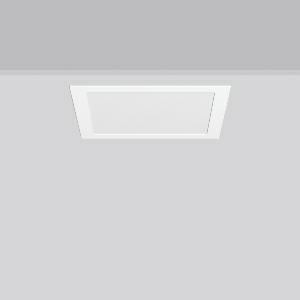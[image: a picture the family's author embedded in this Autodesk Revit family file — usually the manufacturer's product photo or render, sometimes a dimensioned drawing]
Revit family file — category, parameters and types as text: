
# Revit family: toledo_flat_square_e_901488_002_76_2574
name_source: partatom
category: Lighting Fixtures
units: mm (PartAtom-declared; Revit-internal decimal feet)

## family parameters
Cut with Voids When Loaded = No
Host = Face
Light Source = No
Part Type = Normal
Room Calculation Point = No
Round Connector Dimension = Use Diameter
Shared = No

## types (1)
- TOLEDO FLAT square E (1 x LED Modul 830, 2150 lm, 3000)
    Apparent Load = 21 VA
    CIE Flux Codes = 48 80 96 100 100
    Color Rendering = 80
    Color Temperature = 3000
    Default Elevation = 1800 mm
    Description = Series: TOLEDO FLAT square
Ultra thin recessed downlight. Housing: die-cast aluminium. Light guide and diffuser made of non-yellowing PMMA, opal matt. Ceiling installation with spring system. Mounting depth depends on ceiling strength. Suitable for through-wiring with separately available accessories. Surface mounted housing as accessory for all sizes. Retrofittable decorative cylinders made of chintz fabric as accessory, optional with satin finish plastic diffuser. Through-wiring box (5 pole) available as accessory. 
Colour: white
Length: 300 mm
Width: 300 mm
Height: 3 mm
Cut-out length: 280 mm
Cut-out width: 280 mm
Recess height: 31-56 mm
Luminaire: recess height: 31-51 mm
Lamp: LED
Socket: without socket
Colour temperature: 3000K
Colour rendering index (CRI): 80
System power: 21 W
Rated luminous flux: 2150 lm
Luminous efficiency: 102 lm/W
Control gear: Converter, dimmable, DALI
Protection class: II
Type of protection: IP 54
    Height = 0 mm  [stored 0 ft]
    Lamp = 1 x LED Modul 830
    Lamp Light Flux = 2150 lm
    Lamp count = 1
    Length = 300 mm
    Lifetime = 50000 h
    Luminous efficacy = 102 lm/W
    Manufacturer = RZB
    ModVariant = No
    Model = 901488.002.76
    Mounting Place = Ceiling
    Mounting Type = Recessed
    Number of Poles = 1
    OnlyDefault = Yes
    Power Factor = 1
    Product Name = TOLEDO FLAT square E
    Product group = Recessed downlights
    ProductGroupID = 402
    Protection Class = Protection class II
    Protection Degree = IP 20
    RLX_Detail_Level = 1
    RLX_Emergency_Light_Flux = 0 lm
    RLX_Emergency_Type = 0
    RLX_Emergency_Type_DB = No
    RlxData = <blob elided: 60829 chars, md5=9f386e39>
    Socket = socket
    Standby Power = 0 W
    System Light Flux = 2150 lm
    System Power = 21 W
    Type Comments = Product without accessories
    Type Image = 901488.002.jpg
    URL = http://relux.com
    VarID = ---
    Voltage = 230 V
    Voltage Range = 220-240 V
    Weight = 0.00 kg
    Width = 300 mm

note: [stored X ft] marks values corroborated as IEEE doubles in the binary element streams (Revit-internal decimal feet)

## geometry (parser evidence)
native form markers: Blend x4, Sweep x11
no freeform markers — native parametric forms only
